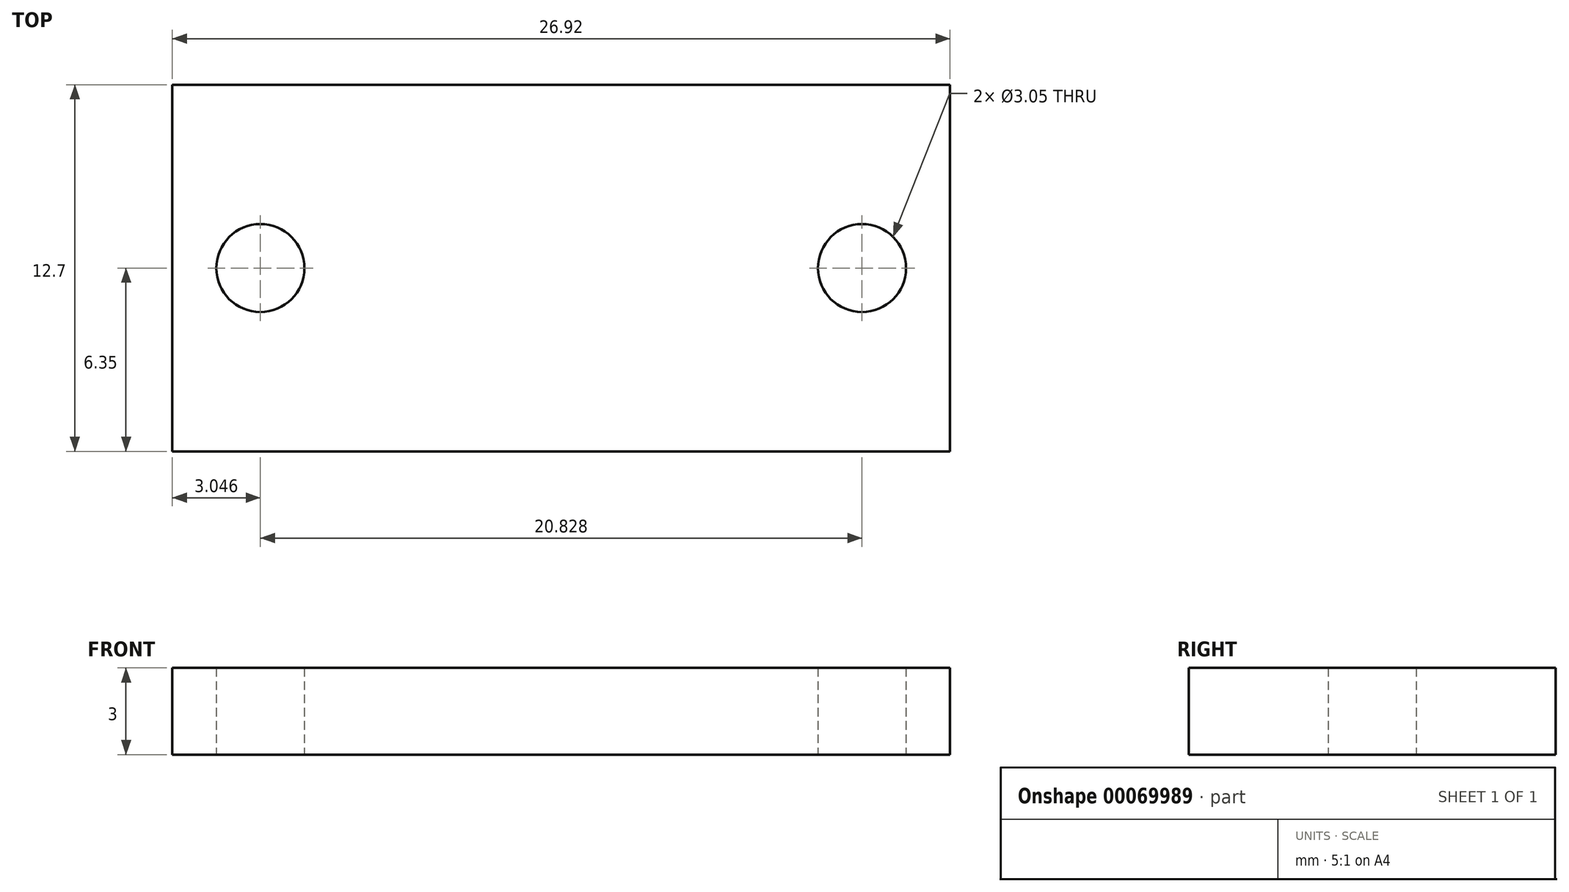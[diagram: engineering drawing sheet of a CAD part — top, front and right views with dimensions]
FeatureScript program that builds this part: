
annotation { "Feature Type Name" : "Feature", "Feature Type Description" : "" }
export const myFeature = defineFeature(function(context is Context, id is Id, definition is map)
    precondition{}
    {
        {
            var Q0;
            Q0=qCreatedBy(makeId("Top.planeOp"),FACE);
            var sketch = newSketch(context, id + "F0", { "sketchPlane" : qUnion([Q0])});
            skLineSegment(sketch, "E0.bottom", {"start": v(-13.46, 6.35) * mm, "end": v(13.46, 6.35) * mm});
            skLineSegment(sketch, "E0.top", {"start": v(-13.46, -6.35) * mm, "end": v(13.46, -6.35) * mm});
            skLineSegment(sketch, "E0.left", {"start": v(-13.46, 6.35) * mm, "end": v(-13.46, -6.35) * mm});
            skLineSegment(sketch, "E0.right", {"start": v(13.46, 6.35) * mm, "end": v(13.46, -6.35) * mm});
            skLineSegment(sketch, "E1", {"start": v(-13.46, 0) * mm, "end": v(13.46, 0) * mm, "construction": true});
            skPoint(sketch, "E2", {"position": v(0, 0) * mm});
            skCircle(sketch, "E3", {"center": v(-10.41, 0) * mm, "radius": 1.52 * mm});
            skCircle(sketch, "E4", {"center": v(10.41, 0) * mm, "radius": 1.52 * mm});
            skSolve(sketch);
        }
        {
            var Q0;
            Q0 = qSketchRegion(id + "F0", true);
            extrude(context, id + "F1", {"entities" : qUnion([Q0]), "depth" : 3 * mm});
        }
    });
